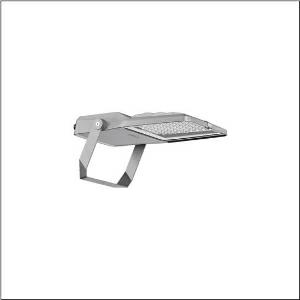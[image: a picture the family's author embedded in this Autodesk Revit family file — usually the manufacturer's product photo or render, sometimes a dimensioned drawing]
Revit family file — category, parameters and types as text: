
# Revit family: floodlight_fl_21_iq_mini___pl52_5xa7771d2d1a_936e
name_source: partatom
category: Lighting Fixtures
units: mm (PartAtom-declared; Revit-internal decimal feet)

## family parameters
Cut with Voids When Loaded = No
Host = Face
Light Source = No
Part Type = Normal
Room Calculation Point = No
Round Connector Dimension = Use Diameter
Shared = No

## types (1)
- --- (1 x LED, 17830 lm, 143 W, 3000K)
    Apparent Load = 143 VA
    CIE Flux Codes = 26 60 98 100 100
    Color Rendering = 70
    Color Temperature = 3000K
    Default Elevation = 1800 mm
    Description = Floodlight FL 21 iQ mini, floodlight, primary light control with lens, of PMMA, primary optical cover: protective disc, of toughened safety glass, transparent, light distribution: PL52, light emission: direct distribution, installation type: surface-mounted, LED, High Power LED, rated luminous flux: 17.830lm, luminous efficacy: 125lm/W, light colour: 730, colour temperature: 3000K, control gear: iQ Comfort/DALI, control: Auto-Match, Temp-Guard, Lumen-Switch, Night-Set, Smart-Wire, Light-Fading, Desk-Remote (wireless, voltage-free reading and setting of iQ features in the workshop via application-optimized NFC function/RFID function), optimised constant luminous flux control (CLO 2.0), with terminal, 6-pole, mains connection: 220..240V, AC, 50/60Hz, start of lifetime: 143W, end of service life: 152W, reduction: 61W, luminaire housing, of diecast aluminium, powder-coated, Siteco® metallic grey (DB 702S), corrosivity category C5 mid according to DIN EN ISO 12944, suitable for swimming pools, chlorine-resistant, sealing non-destructively replaceable, mounting bracket, of steel, galvanised, powder-coated, Siteco® metallic grey (DB 702S), protection rating (complete): IP66, insulation class (complete): insulation class II (safety insulation), certification: CE, ENEC, VDE, protection symbol: D, impact resistance: IK08, permissible operating ambient temperature: -40..+40°C, permissible operating ambient temperature for outdoor applications: -40..+50°C, standard: DIN EN 12944, LABS conformity tested according to VDMA 24364:2018-05, packaging unit: 1 piece

Light Distribution: PL52
    Height = 70 mm
    Lamp = 1 x LED
    Lamp Light Flux = 17830 lm
    Lamp Power = 143 W
    Lamp count = 1
    Length = 485 mm
    Luminous efficacy = 125 lm/W
    Manufacturer = Siteco
    ModVariant = No
    Model = 5XA7771D2D1A
    Number of Poles = 1
    OnlyDefault = Yes
    Power Factor = 1
    Product Name = Floodlight FL 21 iQ mini | PL52
    Product group = floodlight | pylon annexe
    ProductGroupID = 6200
    Protection Class = Protection class II
    Protection Degree = IP 66
    RLX_Detail_Level = 1
    RLX_Emergency_Light_Flux = 0 lm
    RLX_Emergency_Type = 0
    RLX_Emergency_Type_DB = No
    RlxData = <blob elided: 96909 chars, md5=72559b44>
    Socket = socket
    Standby Power = 0 W
    System Light Flux = 17830 lm
    System Power = 143 W
    Type Comments = factory setting: luminous flux: 100 % | dim-lin: 254 | 730 mA
    Type Image = l_1006845.jpg
    URL = http://relux.com
    VarID = @adj_164054
    Voltage = 0 V
    Weight = 0.00 kg
    Width = 337 mm

## geometry (parser evidence)
native form markers: Blend x4, Sweep x13
no freeform markers — native parametric forms only
